# Revit family: BVN_ARMO-R
name_source: partatom
category: Mechanical Equipment
units: mm (PartAtom-declared; Revit-internal decimal feet)

## family parameters
Cut with Voids When Loaded = No
Host = Face
Part Type = Normal
Room Calculation Point = No
Round Connector Dimension = Use Diameter
Shared = No

## types (21) — shared parameters
Default Elevation = 1219 mm
Description = Smoke Exhaust Fan
F = 50 mm  [stored 0.164042 ft]
Manufacturer = Bahçıvan Elektrik Motor San. ve Tic. Ltd. Şti.
Material = <By Category>
Model = ARMO-R
URL = http://www.bahcivanmotor.com.tr

## per-type parameters (varying)
| type | A | Air Flow | B | C | C' | Current | D | E | H | Power | QE | Speed(d/d) | TBH | TBQ | TBQ' | TH | TTBH | TTH | TTT_H | Tepe_Genislik | Wing Angle (Degree) |
| ARMO-R 400-6/1,5-2A | 600 mm | 8978 m³/h | 495 mm  [stored 1.62402 ft] | 702 mm | 552 mm  [stored 1.81102 ft] | 3 A | 400 mm  [stored 1.31234 ft] | 474 mm  [stored 1.55512 ft] | 880 mm | 1500 W | 500 mm  [stored 1.64042 ft] | 2900 | 196 mm | 550 mm | 600 mm | 356 mm  [stored 1.16798 ft] | 96 mm | 160 mm | 64 mm | 251 mm  [stored 0.823491 ft] | 30 |
| ARMO-R 450-6/3-2A | 650 mm  [stored 2.13255 ft] | 13545 m³/h | 545 mm  [stored 1.78806 ft] | 702 mm | 552 mm  [stored 1.81102 ft] | 6 A | 450 mm  [stored 1.47638 ft] | 474 mm  [stored 1.55512 ft] | 880 mm | 3000 W | 550 mm | 2900 | 196 mm | 600 mm | 650 mm  [stored 2.13255 ft] | 356 mm  [stored 1.16798 ft] | 96 mm | 160 mm | 64 mm | 251 mm  [stored 0.823491 ft] | 28 |
| ARMO-R 500-6/4-2A | 650 mm  [stored 2.13255 ft] | 17325 m³/h | 545 mm  [stored 1.78806 ft] | 842 mm | 692 mm | 7 A | 500 mm  [stored 1.64042 ft] | 580 mm  [stored 1.90289 ft] | 1030 mm | 4000 W | 550 mm | 2900 | 220 mm | 600 mm | 650 mm  [stored 2.13255 ft] | 400 mm  [stored 1.31234 ft] | 108 mm | 180 mm | 72 mm | 321 mm  [stored 1.05315 ft] | 26 |
| ARMO-R 560-6/5,5-2A | 685 mm | 22313 m³/h | 605 mm  [stored 1.98491 ft] | 842 mm | 692 mm | 11 A | 560 mm  [stored 1.83727 ft] | 580 mm  [stored 1.90289 ft] | 1030 mm | 5500 W | 585 mm  [stored 1.91929 ft] | 2900 | 220 mm | 635 mm  [stored 2.08333 ft] | 685 mm | 400 mm  [stored 1.31234 ft] | 108 mm | 180 mm | 72 mm | 321 mm  [stored 1.05315 ft] | 20 |
| ARMO-R 630-6/4-4A | 780 mm | 25200 m³/h | 637 mm  [stored 2.0899 ft] | 1130 mm | 980 mm | 8 A | 630 mm  [stored 2.06693 ft] | 600 mm | 1160 mm | 4000 W | 680 mm | 1500 | 281 mm | 730 mm | 780 mm | 510 mm | 138 mm | 230 mm | 92 mm | 465 mm  [stored 1.52559 ft] | 38 |
| ARMO-R 710-6/3-4A | 830 mm | 28350 m³/h | 710 mm | 1130 mm | 980 mm | 7 A | 800 mm | 700 mm | 1300 mm | 3000 W | 720 mm | 1410 | 303 mm | 770 mm | 820 mm | 550 mm | 149 mm | 248 mm | 99 mm | 465 mm  [stored 1.52559 ft] | 28 |
| ARMO-R 800-9/7,5-4A | 920 mm | 40950 m³/h | 800 mm | 1130 mm | 980 mm | 15 A | 800 mm | 700 mm | 1300 mm | 7500 W | 800 mm | 1440 | 303 mm | 850 mm | 900 mm | 550 mm | 149 mm | 248 mm | 99 mm | 465 mm  [stored 1.52559 ft] | 30 |
| ARMO-R 900-9/15-4A | 1020 mm | 63525 m³/h | 900 mm | 1130 mm | 980 mm | 29 A | 900 mm | 775 mm | 1375 mm | 15000 W | 900 mm | 1450 | 303 mm | 950 mm | 1000 mm | 550 mm | 149 mm | 248 mm | 99 mm | 465 mm  [stored 1.52559 ft] | 32 |
| ARMO-R 1000-9/30-4A | 1130 mm | 86100 m³/h | 1030 mm | 1430 mm | 1280 mm | 55 A | 1000 mm | 850 mm | 1450 mm | 30000 W | 1000 mm | 1460 | 303 mm | 1050 mm | 1100 mm | 550 mm | 149 mm | 248 mm | 99 mm | 615 mm  [stored 2.01772 ft] | 32 |
| ARMO-R 1250-9/45-4A | 1430 mm | 138600 m³/h | 1350 mm | 1430 mm | 1280 mm | 80 A | 1250 mm | 950 mm | 1550 mm | 45000 W | 1100 mm | 1475 | 303 mm | 1150 mm | 1200 mm | 550 mm | 149 mm | 248 mm | 99 mm | 615 mm  [stored 2.01772 ft] | 24 |
| ARMO-R 500-6/1,1-4A | 650 mm  [stored 2.13255 ft] | 12600 m³/h | 545 mm  [stored 1.78806 ft] | 842 mm | 692 mm | 3 A | 500 mm  [stored 1.64042 ft] | 580 mm  [stored 1.90289 ft] | 1030 mm | 1100 W | 550 mm | 1400 | 220 mm | 600 mm | 650 mm  [stored 2.13255 ft] | 400 mm  [stored 1.31234 ft] | 108 mm | 180 mm | 72 mm | 321 mm  [stored 1.05315 ft] | 38 |
| ARMO-R 560-6/2,2-4A | 685 mm | 17850 m³/h | 605 mm  [stored 1.98491 ft] | 842 mm | 692 mm | 5 A | 560 mm  [stored 1.83727 ft] | 580 mm  [stored 1.90289 ft] | 1030 mm | 2200 W | 585 mm  [stored 1.91929 ft] | 1410 | 220 mm | 635 mm  [stored 2.08333 ft] | 685 mm | 400 mm  [stored 1.31234 ft] | 108 mm | 180 mm | 72 mm | 321 mm  [stored 1.05315 ft] | 38 |
| ARMO-R 630-6/7,5-2A | 780 mm | 27300 m³/h | 637 mm  [stored 2.0899 ft] | 1130 mm | 980 mm | 14 A | 630 mm  [stored 2.06693 ft] | 600 mm | 1160 mm | 7500 W | 680 mm | 2800 | 281 mm | 730 mm | 780 mm | 510 mm | 138 mm | 230 mm | 92 mm | 465 mm  [stored 1.52559 ft] | 16 |
| ARMO-R 500-6/0,37-6A | 650 mm  [stored 2.13255 ft] | 8400 m³/h | 545 mm  [stored 1.78806 ft] | 842 mm | 692 mm | 1 A | 500 mm  [stored 1.64042 ft] | 580 mm  [stored 1.90289 ft] | 1030 mm | 370 W | 550 mm | 900 | 220 mm | 600 mm | 650 mm  [stored 2.13255 ft] | 400 mm  [stored 1.31234 ft] | 108 mm | 180 mm | 72 mm | 321 mm  [stored 1.05315 ft] | 38 |
| ARMO-R 560-6/0,55-6A | 685 mm | 11760 m³/h | 605 mm  [stored 1.98491 ft] | 842 mm | 692 mm | 2 A | 560 mm  [stored 1.83727 ft] | 580 mm  [stored 1.90289 ft] | 1030 mm | 550 W | 585 mm  [stored 1.91929 ft] | 930 | 220 mm | 635 mm  [stored 2.08333 ft] | 685 mm | 400 mm  [stored 1.31234 ft] | 108 mm | 180 mm | 72 mm | 321 mm  [stored 1.05315 ft] | 38 |
| ARMO-R 630-6/1,1-6A | 780 mm | 16800 m³/h | 637 mm  [stored 2.0899 ft] | 1130 mm | 980 mm | 3 A | 630 mm  [stored 2.06693 ft] | 600 mm | 1160 mm | 1100 W | 680 mm | 945 | 281 mm | 730 mm | 780 mm | 510 mm | 138 mm | 230 mm | 92 mm | 465 mm  [stored 1.52559 ft] | 38 |
| ARMO-R 710-6/3-6A | 830 mm | 18900 m³/h | 710 mm | 1130 mm | 980 mm | 7 A | 800 mm | 700 mm | 1300 mm | 3000 W | 720 mm | 950 | 303 mm | 770 mm | 820 mm | 550 mm | 149 mm | 248 mm | 99 mm | 465 mm  [stored 1.52559 ft] | 28 |
| ARMO-R 800-9/3-6A | 920 mm | 28350 m³/h | 800 mm | 1130 mm | 980 mm | 7 A | 800 mm | 700 mm | 1300 mm | 3000 W | 800 mm | 950 | 303 mm | 850 mm | 900 mm | 550 mm | 149 mm | 248 mm | 99 mm | 465 mm  [stored 1.52559 ft] | 32 |
| ARMO-R 900-9/4-6A | 1020 mm | 39900 m³/h | 900 mm | 1130 mm | 980 mm | 9 A | 900 mm | 775 mm | 1375 mm | 4000 W | 900 mm | 955 | 303 mm | 950 mm | 1000 mm | 550 mm | 149 mm | 248 mm | 99 mm | 465 mm  [stored 1.52559 ft] | 30 |
| ARMO-R 1000-9/7,5-6A | 1130 mm | 57750 m³/h | 1030 mm | 1430 mm | 1280 mm | 15 A | 1000 mm | 850 mm | 1450 mm | 5500 W | 1000 mm | 960 | 303 mm | 1050 mm | 1100 mm | 550 mm | 149 mm | 248 mm | 99 mm | 615 mm  [stored 2.01772 ft] | 32 |
| ARMO-R 1250-9/15-6A | 1430 mm | 105000 m³/h | 1350 mm | 1430 mm | 1280 mm | 29 A | 1250 mm | 950 mm | 1550 mm | 15000 W | 1100 mm | 965 | 303 mm | 1150 mm | 1200 mm | 550 mm | 149 mm | 248 mm | 99 mm | 615 mm  [stored 2.01772 ft] | 28 |

note: [stored X ft] marks values corroborated as IEEE doubles in the binary element streams (Revit-internal decimal feet)

## geometry (parser evidence)
native form markers: Sweep x3
no freeform markers — native parametric forms only
